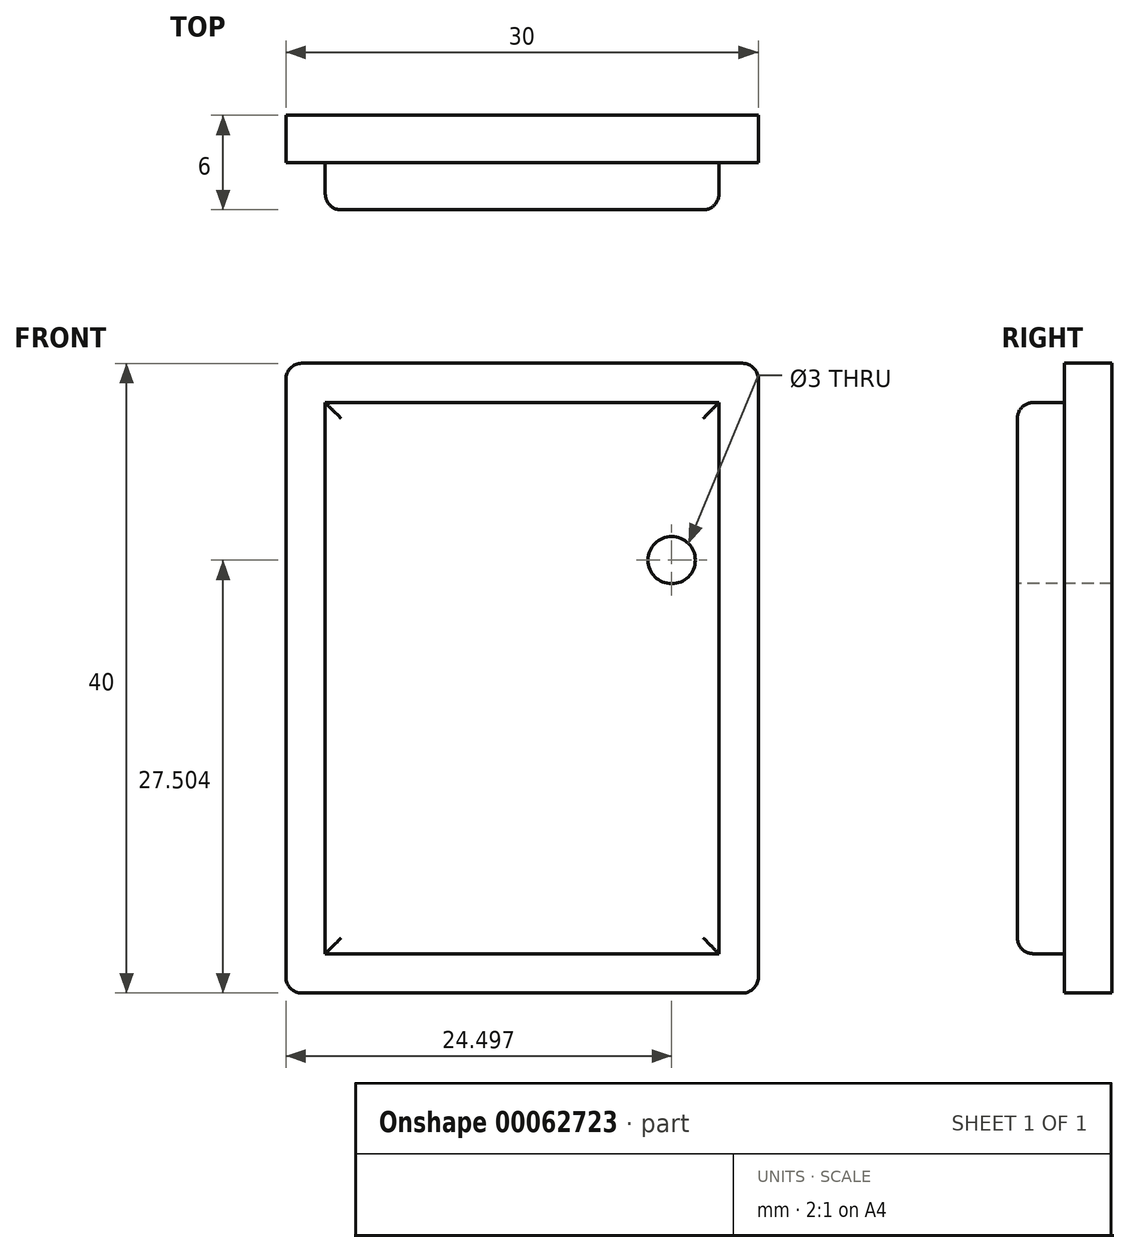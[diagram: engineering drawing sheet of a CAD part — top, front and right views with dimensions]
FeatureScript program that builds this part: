
annotation { "Feature Type Name" : "Feature", "Feature Type Description" : "" }
export const myFeature = defineFeature(function(context is Context, id is Id, definition is map)
    precondition{}
    {
        {
            var Q0;
            Q0=qCreatedBy(makeId("Front.planeOp"),FACE);
            var sketch = newSketch(context, id + "F0", { "sketchPlane" : qUnion([Q0])});
            skLineSegment(sketch, "E0.bottom", {"start": v(-13.07, 30.06) * mm, "end": v(16.93, 30.06) * mm});
            skLineSegment(sketch, "E0.top", {"start": v(-13.07, -9.94) * mm, "end": v(16.93, -9.94) * mm});
            skLineSegment(sketch, "E0.left", {"start": v(-13.07, 30.06) * mm, "end": v(-13.07, -9.94) * mm});
            skLineSegment(sketch, "E0.right", {"start": v(16.93, 30.06) * mm, "end": v(16.93, -9.94) * mm});
            skSolve(sketch);
        }
        {
            var Q0;
            Q0=makeQuery(id+"F0.imprint","IMPRINT",FACE,{"disambiguationData":[TD([[makeQuery(id+"F0.imprint","IMPRINT",EDGE,{"derivedFrom":sQuery(id+"F0.wireOp",EDGE,"E0.bottom")}),-1.0]])]});
            extrude(context, id + "F1", {"entities" : qUnion([Q0]), "depth" : 3 * mm});
        }
        {
            var Q0;
            Q0=makeQuery(id+"F1.opExtrude","CAP_FACE",FACE,{"disambiguationData":[OSD([sQuery(id+"F0.wireOp",EDGE,"E0.bottom"),sQuery(id+"F0.wireOp",EDGE,"E0.top"),sQuery(id+"F0.wireOp",EDGE,"E0.left"),sQuery(id+"F0.wireOp",EDGE,"E0.right")])],"isStart":false});
            var sketch = newSketch(context, id + "F2", { "sketchPlane" : qUnion([Q0])});
            skLineSegment(sketch, "E1.bottom", {"start": v(-10.57, 27.56) * mm, "end": v(14.43, 27.56) * mm});
            skLineSegment(sketch, "E1.top", {"start": v(-10.57, -7.44) * mm, "end": v(14.43, -7.44) * mm});
            skLineSegment(sketch, "E1.left", {"start": v(-10.57, 27.56) * mm, "end": v(-10.57, -7.44) * mm});
            skLineSegment(sketch, "E1.right", {"start": v(14.43, 27.56) * mm, "end": v(14.43, -7.44) * mm});
            skLineSegment(sketch, "E2", {"start": v(-10.57, 27.56) * mm, "end": v(-13.07, 30.06) * mm, "construction": true});
            skLineSegment(sketch, "E3", {"start": v(14.43, 27.56) * mm, "end": v(16.93, 30.06) * mm, "construction": true});
            skLineSegment(sketch, "E4", {"start": v(14.43, -7.44) * mm, "end": v(16.93, -9.94) * mm, "construction": true});
            skSolve(sketch);
        }
        {
            var Q0;
            Q0=makeQuery(id+"F2.imprint","IMPRINT",FACE,{"disambiguationData":[TD([[makeQuery(id+"F2.imprint","IMPRINT",EDGE,{"derivedFrom":sQuery(id+"F2.wireOp",EDGE,"E1.bottom")}),-1.0]])]});
            extrude(context, id + "F3", {"entities" : qUnion([Q0]), "operationType" : NewBodyOperationType.ADD, "depth" : 3 * mm});
        }
        {
            var Q0;
            Q0=makeQuery(id+"F1.opExtrude","SWEPT_EDGE",EDGE,{"disambiguationData":[OSD([sQuery(id+"F0.wireOp",EDGE,"E0.bottom"),sQuery(id+"F0.wireOp",EDGE,"E0.left")])]});
            var Q1;
            Q1=makeQuery(id+"F1.opExtrude","SWEPT_EDGE",EDGE,{"disambiguationData":[OSD([sQuery(id+"F0.wireOp",EDGE,"E0.top"),sQuery(id+"F0.wireOp",EDGE,"E0.left")])]});
            var Q2;
            Q2=makeQuery(id+"F1.opExtrude","SWEPT_EDGE",EDGE,{"disambiguationData":[OSD([sQuery(id+"F0.wireOp",EDGE,"E0.top"),sQuery(id+"F0.wireOp",EDGE,"E0.right")])]});
            var Q3;
            Q3=makeQuery(id+"F1.opExtrude","SWEPT_EDGE",EDGE,{"disambiguationData":[OSD([sQuery(id+"F0.wireOp",EDGE,"E0.bottom"),sQuery(id+"F0.wireOp",EDGE,"E0.right")])]});
            fillet(context, id + "F4", {"entities" : qUnion([Q0, Q1, Q2, Q3]), "radius" : 1 * mm, "tangentPropagation" : true, "allowEdgeOverflow" : false});
        }
        {
            var Q0;
            Q0=makeQuery(id+"F3.opExtrude","CAP_FACE",FACE,{"disambiguationData":[OSD([sQuery(id+"F2.wireOp",EDGE,"E1.bottom"),sQuery(id+"F2.wireOp",EDGE,"E1.top"),sQuery(id+"F2.wireOp",EDGE,"E1.left"),sQuery(id+"F2.wireOp",EDGE,"E1.right")])],"isStart":false});
            fillet(context, id + "F5", {"entities" : qUnion([Q0]), "radius" : 1 * mm, "tangentPropagation" : true, "allowEdgeOverflow" : false});
        }
        {
            var Q0;
            Q0=makeQuery(id+"F3.opExtrude","CAP_FACE",FACE,{"disambiguationData":[OSD([sQuery(id+"F2.wireOp",EDGE,"E1.bottom"),sQuery(id+"F2.wireOp",EDGE,"E1.top"),sQuery(id+"F2.wireOp",EDGE,"E1.left"),sQuery(id+"F2.wireOp",EDGE,"E1.right")])],"isStart":false});
            var sketch = newSketch(context, id + "F6", { "sketchPlane" : qUnion([Q0])});
            skCircle(sketch, "E5", {"center": v(11.43, 17.56) * mm, "radius": 1.5 * mm});
            skSolve(sketch);
        }
        {
            var Q0;
            Q0 = qSketchRegion(id + "F6", true);
            extrude(context, id + "F7", {"entities" : qUnion([Q0]), "operationType" : NewBodyOperationType.REMOVE, "oppositeDirection" : true, "depth" : 25 * mm});
        }
    });
